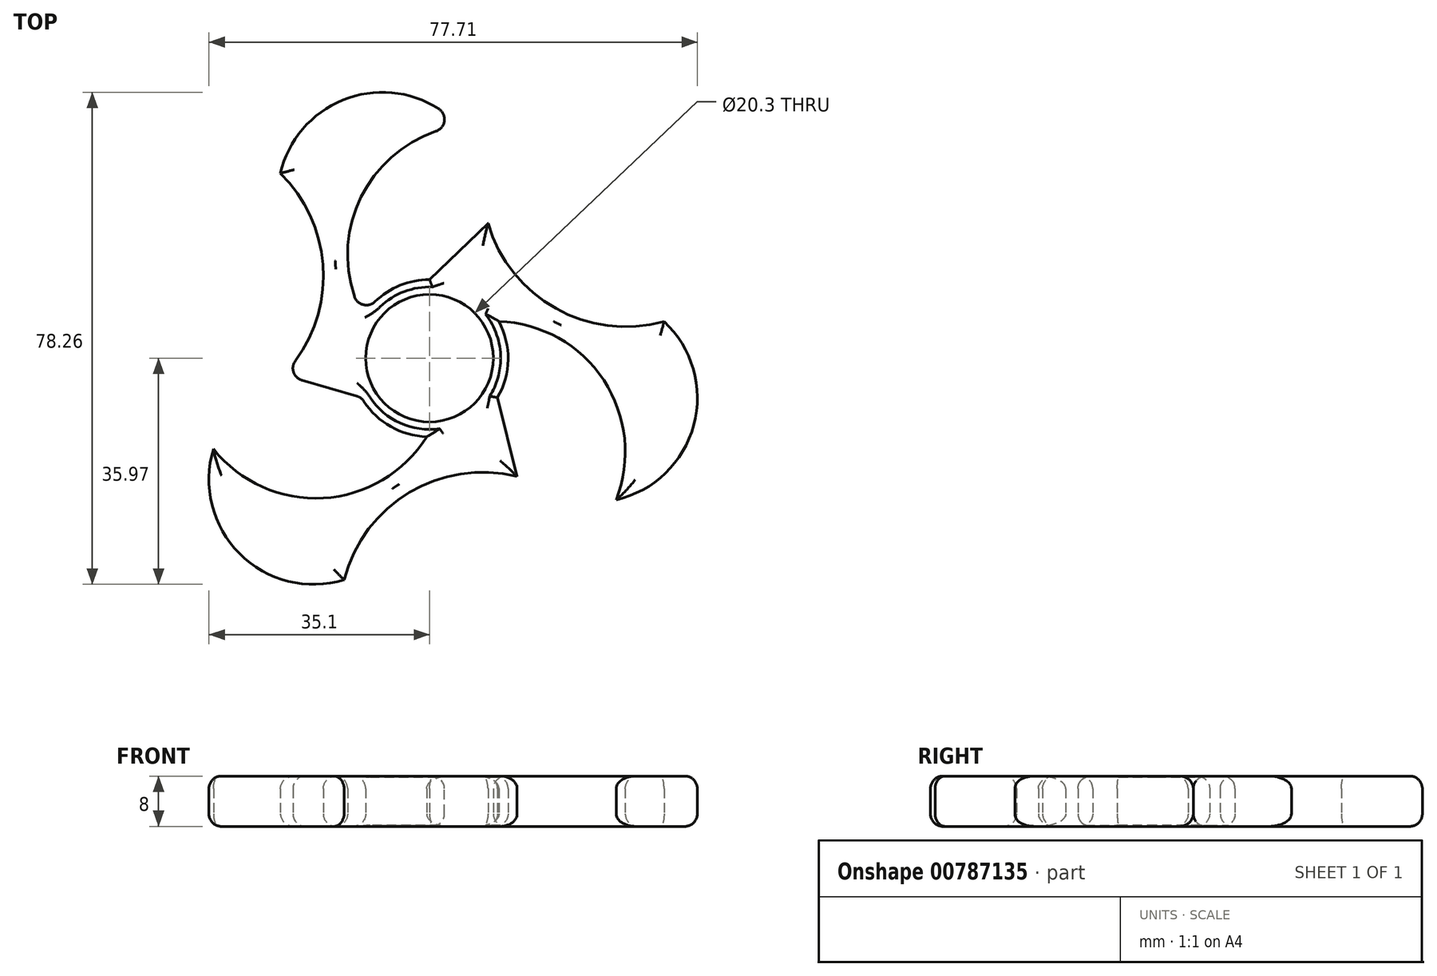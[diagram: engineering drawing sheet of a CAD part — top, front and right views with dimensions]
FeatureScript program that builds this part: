
annotation { "Feature Type Name" : "Feature", "Feature Type Description" : "" }
export const myFeature = defineFeature(function(context is Context, id is Id, definition is map)
    precondition{}
    {
        {
            var Q0;
            Q0=qCreatedBy(makeId("Top.planeOp"),FACE);
            var sketch = newSketch(context, id + "F0", { "sketchPlane" : qUnion([Q0])});
            skCircle(sketch, "E0", {"center": v(0, 0) * mm, "radius": 12.5 * mm});
            skLineSegment(sketch, "E1", {"start": v(0, 12.5) * mm, "end": v(9.31, 21.47) * mm});
            skArc(sketch, "E2", {"start": v(9.31, 21.47) * mm, "mid": v(20.1, 7.9) * mm, "end": v(37.32, 5.85) * mm});
            skArc(sketch, "E3", {"start": v(29.7, -22.54) * mm, "mid": v(42.04, -10.64) * mm, "end": v(37.32, 5.85) * mm});
            skArc(sketch, "E4", {"start": v(29.7, -22.54) * mm, "mid": v(27.73, -3.52) * mm, "end": v(11.05, 5.85) * mm});
            skLineSegment(sketch, "E5.1.0", {"start": v(-10.83, -6.25) * mm, "end": v(-23.25, -2.67) * mm});
            skArc(sketch, "E5.1.1", {"start": v(-23.25, -2.67) * mm, "mid": v(-16.9, 13.46) * mm, "end": v(-23.73, 29.4) * mm});
            skArc(sketch, "E5.1.2", {"start": v(4.67, 37) * mm, "mid": v(-11.8, 41.73) * mm, "end": v(-23.73, 29.4) * mm});
            skArc(sketch, "E5.1.3", {"start": v(4.67, 37) * mm, "mid": v(-10.82, 25.77) * mm, "end": v(-10.59, 6.64) * mm});
            skLineSegment(sketch, "E5.2.0", {"start": v(10.83, -6.25) * mm, "end": v(13.94, -18.8) * mm});
            skArc(sketch, "E5.2.1", {"start": v(13.94, -18.8) * mm, "mid": v(-3.2, -21.37) * mm, "end": v(-13.6, -35.25) * mm});
            skArc(sketch, "E5.2.2", {"start": v(-34.37, -14.45) * mm, "mid": v(-30.23, -31.1) * mm, "end": v(-13.6, -35.25) * mm});
            skArc(sketch, "E5.2.3", {"start": v(-34.37, -14.45) * mm, "mid": v(-16.9, -22.25) * mm, "end": v(-0.46, -12.5) * mm});
            skCircle(sketch, "E6.0", {"center": v(0, 0) * mm, "radius": 10.15 * mm});
            skSolve(sketch);
        }
        {
            var Q0;
            {var subQ0=sQuery(id+"F0.wireOp",EDGE,"E5.1.0");Q0=makeQuery(id+"F0.imprint","IMPRINT",FACE,{"disambiguationData":[TD([[makeQuery(id+"F0.imprint","IMPRINT",EDGE,{"derivedFrom":subQ0}),-1.0]])]});}
            var Q1;
            {var subQ0=sQuery(id+"F0.wireOp",EDGE,"E1");Q1=makeQuery(id+"F0.imprint","IMPRINT",FACE,{"disambiguationData":[TD([[makeQuery(id+"F0.imprint","IMPRINT",EDGE,{"derivedFrom":subQ0}),-1.0]])]});}
            var Q2;
            Q2=makeQuery(id+"F0.imprint","IMPRINT",FACE,{"disambiguationData":[TD([[makeQuery(id+"F0.imprint","IMPRINT",EDGE,{"derivedFrom":sQuery(id+"F0.wireOp",EDGE,"E6.0")}),-1.0]])]});
            var Q3;
            {var subQ0=sQuery(id+"F0.wireOp",EDGE,"E5.2.0");Q3=makeQuery(id+"F0.imprint","IMPRINT",FACE,{"disambiguationData":[TD([[makeQuery(id+"F0.imprint","IMPRINT",EDGE,{"derivedFrom":subQ0}),-1.0]])]});}
            extrude(context, id + "F1", {"entities" : qUnion([Q0, Q1, Q2, Q3]), "depth" : 8 * mm, "offsetDistance" : 25 * mm});
        }
        {
            var Q0;
            Q0=makeQuery(id+"F1.opExtrude","CAP_EDGE",EDGE,{"disambiguationData":[OSD([sQuery(id+"F0.wireOp",EDGE,"E5.1.3")])],"isStart":false});
            var Q1;
            Q1=makeQuery(id+"F1.opExtrude","CAP_EDGE",EDGE,{"disambiguationData":[OSD([sQuery(id+"F0.wireOp",EDGE,"E5.1.2")])],"isStart":false});
            var Q2;
            Q2=makeQuery(id+"F1.opExtrude","CAP_EDGE",EDGE,{"disambiguationData":[OSD([sQuery(id+"F0.wireOp",EDGE,"E5.1.1")])],"isStart":false});
            var Q3;
            Q3=makeQuery(id+"F1.opExtrude","SWEPT_FACE",FACE,{"disambiguationData":[OSD([sQuery(id+"F0.wireOp",EDGE,"E5.1.0")])]});
            var Q4;
            Q4=makeQuery(id+"F1.opExtrude","CAP_EDGE",EDGE,{"disambiguationData":[OSD([sQuery(id+"F0.wireOp",EDGE,"E5.1.1")])],"isStart":true});
            var Q5;
            Q5=makeQuery(id+"F1.opExtrude","CAP_EDGE",EDGE,{"disambiguationData":[OSD([sQuery(id+"F0.wireOp",EDGE,"E5.1.2")])],"isStart":true});
            var Q6;
            Q6=makeQuery(id+"F1.opExtrude","SWEPT_FACE",FACE,{"disambiguationData":[OSD([sQuery(id+"F0.wireOp",EDGE,"E5.1.3")])]});
            var Q7;
            Q7=makeQuery(id+"F1.opExtrude","CAP_EDGE",EDGE,{"disambiguationData":[OSD([sQuery(id+"F0.wireOp",EDGE,"E1")])],"isStart":false});
            var Q8;
            Q8=makeQuery(id+"F1.opExtrude","CAP_FACE",FACE,{"disambiguationData":[OSD([sQuery(id+"F0.wireOp",EDGE,"E0"),sQuery(id+"F0.wireOp",EDGE,"E1"),sQuery(id+"F0.wireOp",EDGE,"E2"),sQuery(id+"F0.wireOp",EDGE,"E3"),sQuery(id+"F0.wireOp",EDGE,"E4"),sQuery(id+"F0.wireOp",EDGE,"E5.1.0"),sQuery(id+"F0.wireOp",EDGE,"E5.1.1"),sQuery(id+"F0.wireOp",EDGE,"E5.1.2"),sQuery(id+"F0.wireOp",EDGE,"E5.1.3"),sQuery(id+"F0.wireOp",EDGE,"E5.2.0"),sQuery(id+"F0.wireOp",EDGE,"E5.2.1"),sQuery(id+"F0.wireOp",EDGE,"E5.2.2"),sQuery(id+"F0.wireOp",EDGE,"E5.2.3"),sQuery(id+"F0.wireOp",EDGE,"E6.0")])],"isStart":false});
            var Q9;
            Q9=makeQuery(id+"F1.opExtrude","CAP_FACE",FACE,{"disambiguationData":[OSD([sQuery(id+"F0.wireOp",EDGE,"E0"),sQuery(id+"F0.wireOp",EDGE,"E1"),sQuery(id+"F0.wireOp",EDGE,"E2"),sQuery(id+"F0.wireOp",EDGE,"E3"),sQuery(id+"F0.wireOp",EDGE,"E4"),sQuery(id+"F0.wireOp",EDGE,"E5.1.0"),sQuery(id+"F0.wireOp",EDGE,"E5.1.1"),sQuery(id+"F0.wireOp",EDGE,"E5.1.2"),sQuery(id+"F0.wireOp",EDGE,"E5.1.3"),sQuery(id+"F0.wireOp",EDGE,"E5.2.0"),sQuery(id+"F0.wireOp",EDGE,"E5.2.1"),sQuery(id+"F0.wireOp",EDGE,"E5.2.2"),sQuery(id+"F0.wireOp",EDGE,"E5.2.3"),sQuery(id+"F0.wireOp",EDGE,"E6.0")])],"isStart":true});
            fillet(context, id + "F2", {"entities" : qUnion([Q0, Q1, Q2, Q3, Q4, Q5, Q6, Q7, Q8, Q9]), "radius" : 2 * mm, "tangentPropagation" : true, "allowEdgeOverflow" : false});
        }
    });
